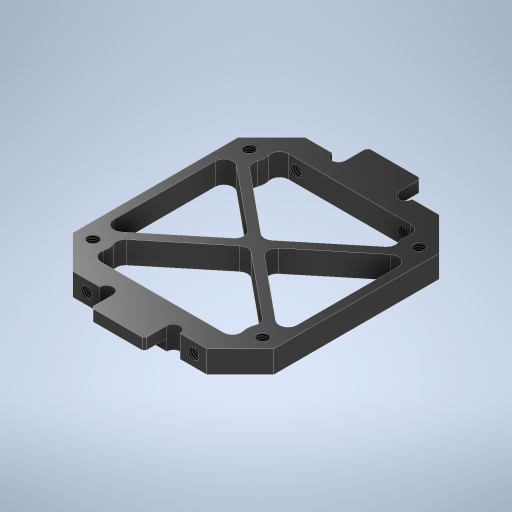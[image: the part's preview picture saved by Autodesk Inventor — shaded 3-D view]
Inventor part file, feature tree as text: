
AUTODESK INVENTOR PART (.ipt)
format: ipt  version: 2024.2 (Build 282272000, 272)  size: 397,312 bytes
history: native  units: mm
features: sketch x2, extrude x2, hole x2, mirror x1, chamfer x1
ambient origin geometry x8: Origin, YZ Plane, XZ Plane, XY Plane, X Axis, Y Axis, Z Axis, Center Point
bodies: Solid1 (feature_tree)
feature tree (8):
  sketch  "Sketch1"  dims[d0=62.0mm d1=45.0mm]
  extrude  "Extrusion1"  Depth=45.0mm
  extrude  "Extrusion2"  Depth=12.0mm
  hole  "Hole1"  [1 undecoded]
  hole  "Hole2"  [1 undecoded]
  mirror  "Mirror1"
  chamfer  "Chamfer1"  Distance=6.0mm
  sketch  "Sketch2"  dims[d2=1.5mm d3=12.0mm d4=5.0mm d5=30.0mm d6=6.0mm d7=3.0mm d8=3.0mm d10=2.0mm d11=2.0mm d12=5.0mm d13=45.0deg d14=2.0mm d16=5.0mm d17=0.0mm d18=2.5mm d19=0.0mm d20=2.459mm d21=6.0mm d22=4.0mm d23=2.0mm d24=90.0deg d25=6.0mm d26=0.0mm d27=2.459mm d28=6.0mm d29=4.0mm d30=2.0mm d31=90.0deg d32=6.0mm d33=0.0mm d36=38.0mm d37=35.0mm d38=2.0mm d39=0.5mm d40=2.0mm d41=45.0deg]
note: 2 required parameter values undecoded (feature->parameter linkage not recoverable at this tier; creation-order binding heuristic only, values carry confidence <= 0.55)
